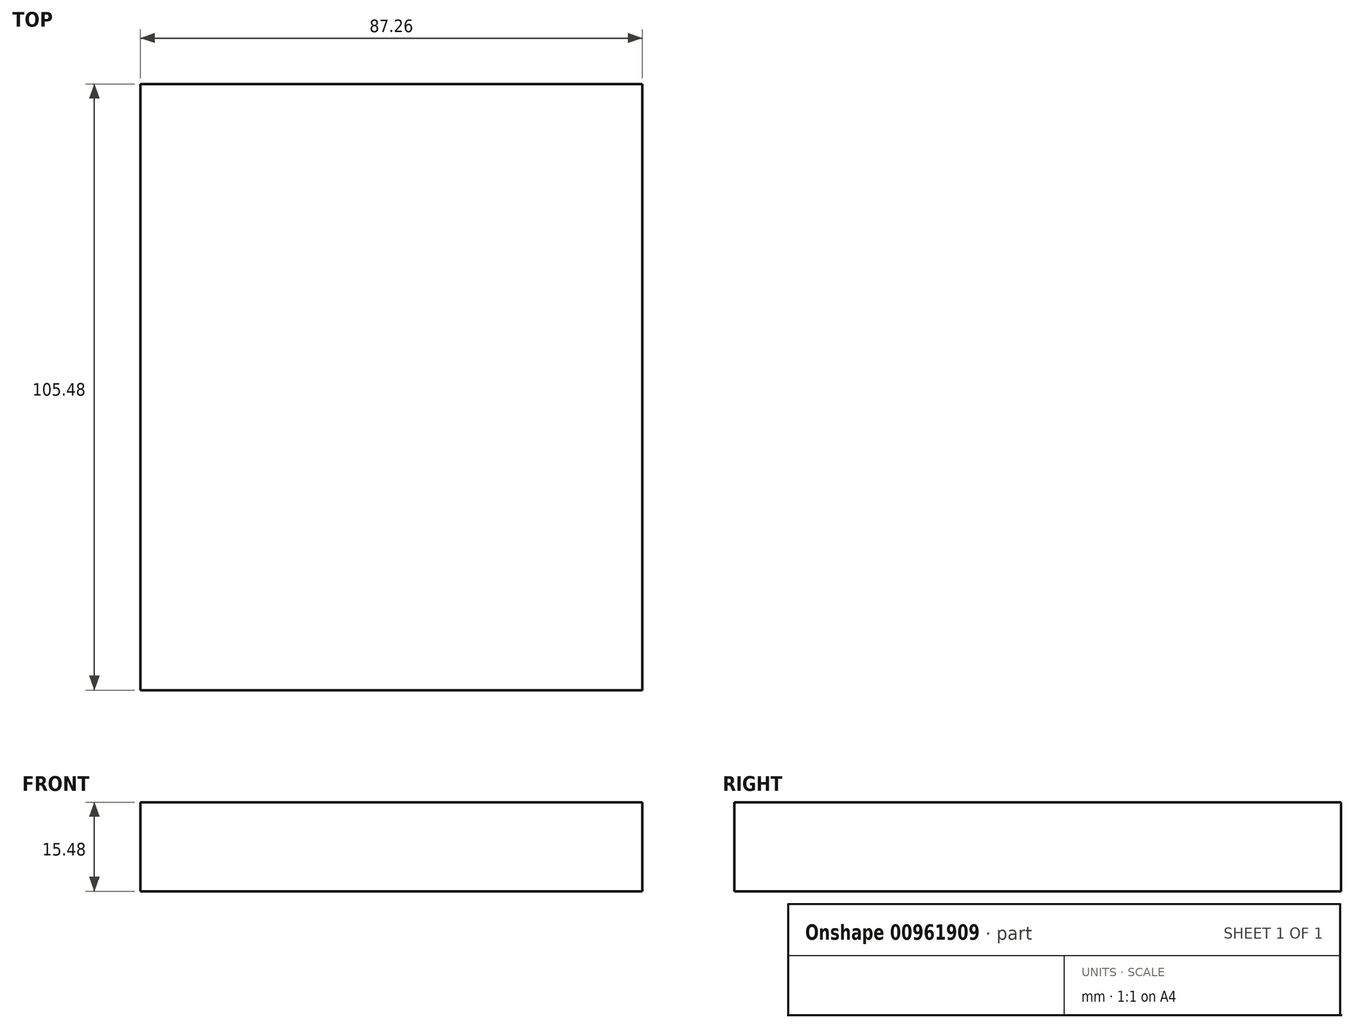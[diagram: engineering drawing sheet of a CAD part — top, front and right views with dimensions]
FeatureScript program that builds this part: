
annotation { "Feature Type Name" : "Feature", "Feature Type Description" : "" }
export const myFeature = defineFeature(function(context is Context, id is Id, definition is map)
    precondition{}
    {
        {
            var Q0;
            Q0=qCreatedBy(makeId("Top.planeOp"),FACE);
            var sketch = newSketch(context, id + "F0", { "sketchPlane" : qUnion([Q0])});
            skLineSegment(sketch, "E0.bottom", {"start": v(-43.63, -52.74) * mm, "end": v(43.63, -52.74) * mm});
            skLineSegment(sketch, "E0.top", {"start": v(-43.63, 52.74) * mm, "end": v(43.63, 52.74) * mm});
            skLineSegment(sketch, "E0.left", {"start": v(-43.63, -52.74) * mm, "end": v(-43.63, 52.74) * mm});
            skLineSegment(sketch, "E0.right", {"start": v(43.63, -52.74) * mm, "end": v(43.63, 52.74) * mm});
            skPoint(sketch, "E0.middle", {"position": v(0, 0) * mm});
            skSolve(sketch);
        }
        {
            var Q0;
            Q0=makeQuery(id+"F0.imprint","IMPRINT",FACE,{"disambiguationData":[TD([[makeQuery(id+"F0.imprint","IMPRINT",EDGE,{"derivedFrom":sQuery(id+"F0.wireOp",EDGE,"E0.bottom")}),1.0]])]});
            var sketch = newSketch(context, id + "F1", { "sketchPlane" : qUnion([Q0])});
            skSolve(sketch);
        }
        {
            var Q0;
            Q0=makeQuery(id+"F1.imprint","IMPRINT",FACE,{"disambiguationData":[TD([[makeQuery(id+"F1.imprint","IMPRINT",EDGE,{"derivedFrom":makeQuery(id+"F0.imprint","IMPRINT",EDGE,{"derivedFrom":sQuery(id+"F0.wireOp",EDGE,"E0.bottom")})}),1.0]])]});
            extrude(context, id + "F2", {"entities" : qUnion([Q0]), "depth" : 15.48 * mm, "offsetDistance" : 25.4 * mm});
        }
    });
